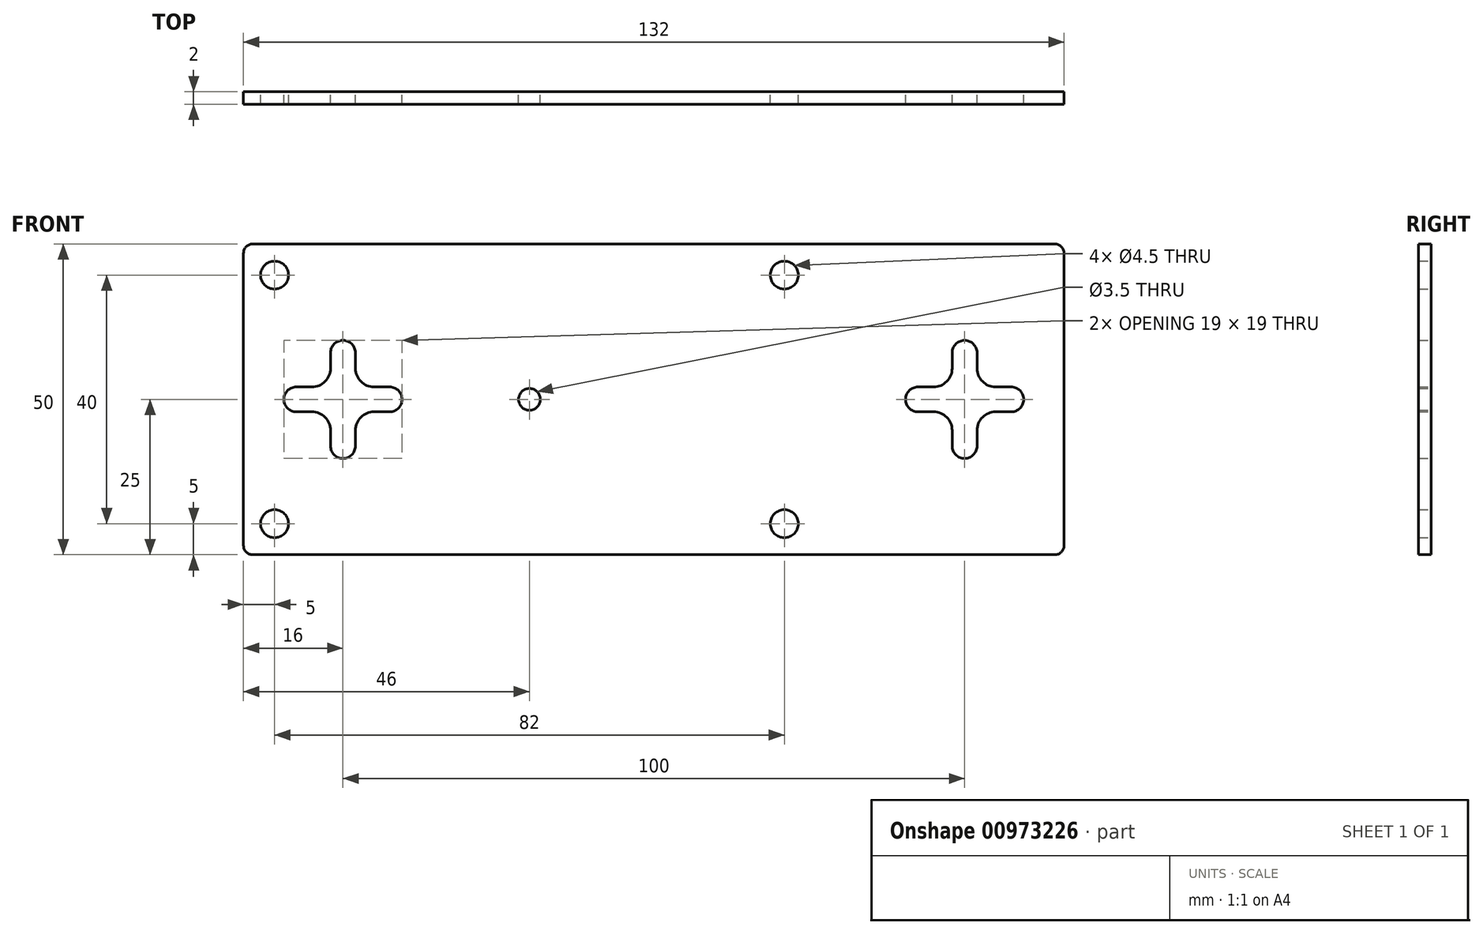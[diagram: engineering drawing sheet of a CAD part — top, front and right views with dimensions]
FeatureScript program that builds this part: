
annotation { "Feature Type Name" : "Feature", "Feature Type Description" : "" }
export const myFeature = defineFeature(function(context is Context, id is Id, definition is map)
    precondition{}
    {
        {
            var Q0;
            Q0=qCreatedBy(makeId("Front.planeOp"),FACE);
            var sketch = newSketch(context, id + "F0", { "sketchPlane" : qUnion([Q0])});
            skLineSegment(sketch, "E0.0", {"start": v(0, 0) * mm, "end": v(0, 50) * mm});
            skLineSegment(sketch, "E0.1", {"start": v(0, 0) * mm, "end": v(132, 0) * mm});
            skLineSegment(sketch, "E0.2", {"start": v(92, 0) * mm, "end": v(92, 50) * mm});
            skLineSegment(sketch, "E0.3", {"start": v(0, 50) * mm, "end": v(132, 50) * mm});
            skCircle(sketch, "E1", {"center": v(5, 45) * mm, "radius": 2.25 * mm});
            skCircle(sketch, "E2", {"center": v(87, 45) * mm, "radius": 2.25 * mm});
            skCircle(sketch, "E3", {"center": v(5, 5) * mm, "radius": 2.25 * mm});
            skCircle(sketch, "E4", {"center": v(87, 5) * mm, "radius": 2.25 * mm});
            skCircle(sketch, "E5", {"center": v(46, 25) * mm, "radius": 1.75 * mm});
            skLineSegment(sketch, "E6", {"start": v(132, 0) * mm, "end": v(132, 50) * mm});
            skLineSegment(sketch, "E7", {"start": v(16, 32.5) * mm, "end": v(16, 17.5) * mm});
            skLineSegment(sketch, "E8", {"start": v(8.5, 25) * mm, "end": v(23.5, 25) * mm});
            skArc(sketch, "E9.0.startCap", {"start": v(8.5, 23) * mm, "mid": v(6.5, 25) * mm, "end": v(8.5, 27) * mm});
            skArc(sketch, "E9.0.endCap", {"start": v(23.5, 27) * mm, "mid": v(25.5, 25) * mm, "end": v(23.5, 23) * mm});
            skLineSegment(sketch, "E9.0.left", {"start": v(8.5, 27) * mm, "end": v(23.5, 27) * mm});
            skLineSegment(sketch, "E9.0.right", {"start": v(8.5, 23) * mm, "end": v(23.5, 23) * mm});
            skArc(sketch, "E9.1.startCap", {"start": v(14, 32.5) * mm, "mid": v(16, 34.5) * mm, "end": v(18, 32.5) * mm});
            skArc(sketch, "E9.1.endCap", {"start": v(18, 17.5) * mm, "mid": v(16, 15.5) * mm, "end": v(14, 17.5) * mm});
            skLineSegment(sketch, "E9.1.left", {"start": v(18, 32.5) * mm, "end": v(18, 17.5) * mm});
            skLineSegment(sketch, "E9.1.right", {"start": v(14, 32.5) * mm, "end": v(14, 17.5) * mm});
            skLineSegment(sketch, "E10.1.0.0", {"start": v(114, 32.5) * mm, "end": v(114, 17.5) * mm});
            skLineSegment(sketch, "E10.1.0.1", {"start": v(108.5, 27) * mm, "end": v(123.5, 27) * mm});
            skArc(sketch, "E10.1.0.2", {"start": v(123.5, 27) * mm, "mid": v(125.5, 25) * mm, "end": v(123.5, 23) * mm});
            skArc(sketch, "E10.1.0.3", {"start": v(118, 17.5) * mm, "mid": v(116, 15.5) * mm, "end": v(114, 17.5) * mm});
            skLineSegment(sketch, "E10.1.0.4", {"start": v(116, 32.5) * mm, "end": v(116, 17.5) * mm});
            skLineSegment(sketch, "E10.1.0.5", {"start": v(108.5, 25) * mm, "end": v(123.5, 25) * mm});
            skLineSegment(sketch, "E10.1.0.6", {"start": v(108.5, 23) * mm, "end": v(123.5, 23) * mm});
            skArc(sketch, "E10.1.0.7", {"start": v(114, 32.5) * mm, "mid": v(116, 34.5) * mm, "end": v(118, 32.5) * mm});
            skArc(sketch, "E10.1.0.8", {"start": v(108.5, 23) * mm, "mid": v(106.5, 25) * mm, "end": v(108.5, 27) * mm});
            skLineSegment(sketch, "E10.1.0.9", {"start": v(118, 32.5) * mm, "end": v(118, 17.5) * mm});
            skLineSegment(sketch, "E10.direction1", {"start": v(14, 17.5) * mm, "end": v(114, 17.5) * mm, "construction": true});
            skLineSegment(sketch, "E11.filletArc", {"start": v(132, 50) * mm, "end": v(132, 50) * mm});
            skLineSegment(sketch, "E12.filletArc", {"start": v(132, 0) * mm, "end": v(132, 0) * mm});
            skSolve(sketch);
        }
        {
            var Q0;
            Q0=makeQuery(id+"F0.imprint","IMPRINT",FACE,{"disambiguationData":[TD([[makeQuery(id+"F0.imprint","IMPRINT",EDGE,{"derivedFrom":sQuery(id+"F0.wireOp",EDGE,"E1")}),-1.0]])]});
            var Q1;
            Q1=makeQuery(id+"F0.imprint","IMPRINT",FACE,{"disambiguationData":[TD([[makeQuery(id+"F0.imprint","IMPRINT",EDGE,{"derivedFrom":sQuery(id+"F0.wireOp",EDGE,"E3")}),-1.0]])]});
            var Q2;
            Q2=makeQuery(id+"F0.imprint","IMPRINT",FACE,{"disambiguationData":[TD([[makeQuery(id+"F0.imprint","IMPRINT",EDGE,{"derivedFrom":sQuery(id+"F0.wireOp",EDGE,"E4")}),-1.0]])]});
            var Q3;
            Q3=makeQuery(id+"F0.imprint","IMPRINT",FACE,{"disambiguationData":[TD([[makeQuery(id+"F0.imprint","IMPRINT",EDGE,{"derivedFrom":sQuery(id+"F0.wireOp",EDGE,"E2")}),-1.0]])]});
            var Q4;
            {var subQ0=sQuery(id+"F0.wireOp",EDGE,"xmzwrryO-BlZN-0bC2-PON8-yqqjyzBsKTHA");var subQ1=sQuery(id+"F0.wireOp",EDGE,"6Q67PZT9-bBxg-zhkt-OXOf-C5b4L4PpcKHw");var subQ2=makeQuery(id+"F0.imprint","INTERSECT",VERTEX,{"disambiguationData":[OD(0.0)],"derivedFrom":[subQ1,subQ0]});Q4=makeQuery(id+"F0.imprint","IMPRINT",FACE,{"disambiguationData":[TD([[makeQuery(id+"F0.imprint","IMPRINT",EDGE,{"disambiguationData":[TD([[subQ2,-1.0]])],"derivedFrom":subQ1}),-1.0]])]});}
            var Q5;
            {var subQ0=sQuery(id+"F0.wireOp",EDGE,"xmzwrryO-BlZN-0bC2-PON8-yqqjyzBsKTHA");var subQ1=sQuery(id+"F0.wireOp",EDGE,"6Q67PZT9-bBxg-zhkt-OXOf-C5b4L4PpcKHw");var subQ2=makeQuery(id+"F0.imprint","INTERSECT",VERTEX,{"disambiguationData":[OD(0.0)],"derivedFrom":[subQ1,subQ0]});Q5=makeQuery(id+"F0.imprint","IMPRINT",FACE,{"disambiguationData":[TD([[makeQuery(id+"F0.imprint","IMPRINT",EDGE,{"disambiguationData":[TD([[subQ2,-1.0]])],"derivedFrom":subQ1}),1.0]])]});}
            var Q6;
            {var subQ0=sQuery(id+"F0.wireOp",EDGE,"ZZCkcGhh-moAk-lj8j-4bvt-TYEpWencMZMl");var subQ1=sQuery(id+"F0.wireOp",EDGE,"NE1wQv6m-4w3k-G8xB-BjyB-1MqrszNTXdfy");var subQ2=makeQuery(id+"F0.imprint","INTERSECT",VERTEX,{"disambiguationData":[OD(0.0)],"derivedFrom":[subQ1,subQ0]});Q6=makeQuery(id+"F0.imprint","IMPRINT",FACE,{"disambiguationData":[TD([[makeQuery(id+"F0.imprint","IMPRINT",EDGE,{"disambiguationData":[TD([[subQ2,-1.0]])],"derivedFrom":subQ1}),-1.0]])]});}
            var Q7;
            {var subQ0=sQuery(id+"F0.wireOp",EDGE,"ZZCkcGhh-moAk-lj8j-4bvt-TYEpWencMZMl");var subQ1=sQuery(id+"F0.wireOp",EDGE,"NE1wQv6m-4w3k-G8xB-BjyB-1MqrszNTXdfy");var subQ2=makeQuery(id+"F0.imprint","INTERSECT",VERTEX,{"disambiguationData":[OD(0.0)],"derivedFrom":[subQ1,subQ0]});Q7=makeQuery(id+"F0.imprint","IMPRINT",FACE,{"disambiguationData":[TD([[makeQuery(id+"F0.imprint","IMPRINT",EDGE,{"disambiguationData":[TD([[subQ2,-1.0]])],"derivedFrom":subQ1}),1.0]])]});}
            var Q8;
            {var subQ0=sQuery(id+"F0.wireOp",EDGE,"5zX6bmv4-brnL-wLrf-yGTW-631ojesh5KmC");var subQ1=sQuery(id+"F0.wireOp",EDGE,"6Q67PZT9-bBxg-zhkt-OXOf-C5b4L4PpcKHw");var subQ2=makeQuery(id+"F0.imprint","INTERSECT",VERTEX,{"disambiguationData":[OD(0.0)],"derivedFrom":[subQ1,subQ0]});Q8=makeQuery(id+"F0.imprint","IMPRINT",FACE,{"disambiguationData":[TD([[makeQuery(id+"F0.imprint","IMPRINT",EDGE,{"disambiguationData":[TD([[subQ2,1.0]])],"derivedFrom":subQ1}),1.0]])]});}
            var Q9;
            {var subQ0=sQuery(id+"F0.wireOp",EDGE,"5zX6bmv4-brnL-wLrf-yGTW-631ojesh5KmC");var subQ1=sQuery(id+"F0.wireOp",EDGE,"6Q67PZT9-bBxg-zhkt-OXOf-C5b4L4PpcKHw");var subQ2=makeQuery(id+"F0.imprint","INTERSECT",VERTEX,{"disambiguationData":[OD(0.0)],"derivedFrom":[subQ1,subQ0]});Q9=makeQuery(id+"F0.imprint","IMPRINT",FACE,{"disambiguationData":[TD([[makeQuery(id+"F0.imprint","IMPRINT",EDGE,{"disambiguationData":[TD([[subQ2,1.0]])],"derivedFrom":subQ1}),-1.0]])]});}
            var Q10;
            {var subQ3=sQuery(id+"F0.wireOp",EDGE,"5zX6bmv4-brnL-wLrf-yGTW-631ojesh5KmC");var subQ5=sQuery(id+"F0.wireOp",EDGE,"6Q67PZT9-bBxg-zhkt-OXOf-C5b4L4PpcKHw");var subQ6=makeQuery(id+"F0.imprint","INTERSECT",VERTEX,{"disambiguationData":[OD(0.0)],"derivedFrom":[subQ5,subQ3]});Q10=makeQuery(id+"F0.imprint","IMPRINT",FACE,{"disambiguationData":[TD([[makeQuery(id+"F0.imprint","IMPRINT",EDGE,{"disambiguationData":[TD([[subQ6,-1.0]])],"derivedFrom":subQ5}),-1.0]])]});}
            var Q11;
            {var subQ3=sQuery(id+"F0.wireOp",EDGE,"5zX6bmv4-brnL-wLrf-yGTW-631ojesh5KmC");var subQ5=sQuery(id+"F0.wireOp",EDGE,"6Q67PZT9-bBxg-zhkt-OXOf-C5b4L4PpcKHw");var subQ6=makeQuery(id+"F0.imprint","INTERSECT",VERTEX,{"disambiguationData":[OD(0.0)],"derivedFrom":[subQ5,subQ3]});Q11=makeQuery(id+"F0.imprint","IMPRINT",FACE,{"disambiguationData":[TD([[makeQuery(id+"F0.imprint","IMPRINT",EDGE,{"disambiguationData":[TD([[subQ6,-1.0]])],"derivedFrom":subQ5}),1.0]])]});}
            var Q12;
            {var subQ0=sQuery(id+"F0.wireOp",EDGE,"E5");var subQ5=sQuery(id+"F0.wireOp",EDGE,"6Q67PZT9-bBxg-zhkt-OXOf-C5b4L4PpcKHw");var subQ6=makeQuery(id+"F0.imprint","INTERSECT",VERTEX,{"disambiguationData":[OD(1.0)],"derivedFrom":[subQ5,subQ0]});Q12=makeQuery(id+"F0.imprint","IMPRINT",FACE,{"disambiguationData":[TD([[makeQuery(id+"F0.imprint","IMPRINT",EDGE,{"disambiguationData":[TD([[subQ6,-1.0]])],"derivedFrom":subQ5}),1.0]])]});}
            var Q13;
            {var subQ0=sQuery(id+"F0.wireOp",EDGE,"E5");var subQ5=sQuery(id+"F0.wireOp",EDGE,"6Q67PZT9-bBxg-zhkt-OXOf-C5b4L4PpcKHw");var subQ7=makeQuery(id+"F0.imprint","INTERSECT",VERTEX,{"disambiguationData":[OD(1.0)],"derivedFrom":[subQ5,subQ0]});Q13=makeQuery(id+"F0.imprint","IMPRINT",FACE,{"disambiguationData":[TD([[makeQuery(id+"F0.imprint","IMPRINT",EDGE,{"disambiguationData":[TD([[subQ7,-1.0]])],"derivedFrom":subQ5}),-1.0]])]});}
            var Q14;
            {var subQ0=sQuery(id+"F0.wireOp",EDGE,"5zX6bmv4-brnL-wLrf-yGTW-631ojesh5KmC");var subQ1=sQuery(id+"F0.wireOp",EDGE,"6Q67PZT9-bBxg-zhkt-OXOf-C5b4L4PpcKHw");var subQ2=makeQuery(id+"F0.imprint","INTERSECT",VERTEX,{"disambiguationData":[OD(1.0)],"derivedFrom":[subQ1,subQ0]});Q14=makeQuery(id+"F0.imprint","IMPRINT",FACE,{"disambiguationData":[TD([[makeQuery(id+"F0.imprint","IMPRINT",EDGE,{"disambiguationData":[TD([[subQ2,-1.0]])],"derivedFrom":subQ1}),-1.0]])]});}
            var Q15;
            {var subQ0=sQuery(id+"F0.wireOp",EDGE,"5zX6bmv4-brnL-wLrf-yGTW-631ojesh5KmC");var subQ1=sQuery(id+"F0.wireOp",EDGE,"6Q67PZT9-bBxg-zhkt-OXOf-C5b4L4PpcKHw");var subQ2=makeQuery(id+"F0.imprint","INTERSECT",VERTEX,{"disambiguationData":[OD(1.0)],"derivedFrom":[subQ1,subQ0]});Q15=makeQuery(id+"F0.imprint","IMPRINT",FACE,{"disambiguationData":[TD([[makeQuery(id+"F0.imprint","IMPRINT",EDGE,{"disambiguationData":[TD([[subQ2,-1.0]])],"derivedFrom":subQ1}),1.0]])]});}
            var Q16;
            {var subQ0=sQuery(id+"F0.wireOp",EDGE,"qFN6vZkK-eyPu-iBXI-5w6p-NcDML7FWDEbE");var subQ1=sQuery(id+"F0.wireOp",EDGE,"NE1wQv6m-4w3k-G8xB-BjyB-1MqrszNTXdfy");var subQ2=makeQuery(id+"F0.imprint","INTERSECT",VERTEX,{"disambiguationData":[OD(1.0)],"derivedFrom":[subQ1,subQ0]});Q16=makeQuery(id+"F0.imprint","IMPRINT",FACE,{"disambiguationData":[TD([[makeQuery(id+"F0.imprint","IMPRINT",EDGE,{"disambiguationData":[TD([[subQ2,-1.0]])],"derivedFrom":subQ1}),1.0]])]});}
            var Q17;
            {var subQ0=sQuery(id+"F0.wireOp",EDGE,"qFN6vZkK-eyPu-iBXI-5w6p-NcDML7FWDEbE");var subQ1=sQuery(id+"F0.wireOp",EDGE,"NE1wQv6m-4w3k-G8xB-BjyB-1MqrszNTXdfy");var subQ2=makeQuery(id+"F0.imprint","INTERSECT",VERTEX,{"disambiguationData":[OD(1.0)],"derivedFrom":[subQ1,subQ0]});Q17=makeQuery(id+"F0.imprint","IMPRINT",FACE,{"disambiguationData":[TD([[makeQuery(id+"F0.imprint","IMPRINT",EDGE,{"disambiguationData":[TD([[subQ2,-1.0]])],"derivedFrom":subQ1}),-1.0]])]});}
            var Q18;
            {var subQ0=sQuery(id+"F0.wireOp",EDGE,"xmzwrryO-BlZN-0bC2-PON8-yqqjyzBsKTHA");var subQ1=sQuery(id+"F0.wireOp",EDGE,"6Q67PZT9-bBxg-zhkt-OXOf-C5b4L4PpcKHw");var subQ2=makeQuery(id+"F0.imprint","INTERSECT",VERTEX,{"disambiguationData":[OD(1.0)],"derivedFrom":[subQ1,subQ0]});Q18=makeQuery(id+"F0.imprint","IMPRINT",FACE,{"disambiguationData":[TD([[makeQuery(id+"F0.imprint","IMPRINT",EDGE,{"disambiguationData":[TD([[subQ2,1.0]])],"derivedFrom":subQ1}),-1.0]])]});}
            var Q19;
            {var subQ0=sQuery(id+"F0.wireOp",EDGE,"xmzwrryO-BlZN-0bC2-PON8-yqqjyzBsKTHA");var subQ1=sQuery(id+"F0.wireOp",EDGE,"6Q67PZT9-bBxg-zhkt-OXOf-C5b4L4PpcKHw");var subQ2=makeQuery(id+"F0.imprint","INTERSECT",VERTEX,{"disambiguationData":[OD(1.0)],"derivedFrom":[subQ1,subQ0]});Q19=makeQuery(id+"F0.imprint","IMPRINT",FACE,{"disambiguationData":[TD([[makeQuery(id+"F0.imprint","IMPRINT",EDGE,{"disambiguationData":[TD([[subQ2,1.0]])],"derivedFrom":subQ1}),1.0]])]});}
            var Q20;
            {var subQ12=sQuery(id+"F0.wireOp",EDGE,"E0.2");Q20=makeQuery(id+"F0.imprint","IMPRINT",FACE,{"disambiguationData":[TD([[makeQuery(id+"F0.imprint","IMPRINT",EDGE,{"derivedFrom":subQ12}),-1.0]])]});}
            extrude(context, id + "F1", {"entities" : qUnion([Q0, Q1, Q2, Q3, Q4, Q5, Q6, Q7, Q8, Q9, Q10, Q11, Q12, Q13, Q14, Q15, Q16, Q17, Q18, Q19, Q20]), "depth" : 2 * mm, "offsetDistance" : 25 * mm});
        }
        {
            var Q0;
            Q0=makeQuery(id+"F1.opExtrude","SWEPT_EDGE",EDGE,{"disambiguationData":[OSD([sQuery(id+"F0.wireOp",EDGE,"E9.0.left"),sQuery(id+"F0.wireOp",EDGE,"E9.1.right")])]});
            var Q1;
            Q1=makeQuery(id+"F1.opExtrude","SWEPT_EDGE",EDGE,{"disambiguationData":[OSD([sQuery(id+"F0.wireOp",EDGE,"E9.0.right"),sQuery(id+"F0.wireOp",EDGE,"E9.1.right")])]});
            var Q2;
            Q2=makeQuery(id+"F1.opExtrude","SWEPT_EDGE",EDGE,{"disambiguationData":[OSD([sQuery(id+"F0.wireOp",EDGE,"E9.0.left"),sQuery(id+"F0.wireOp",EDGE,"E9.1.left")])]});
            var Q3;
            Q3=makeQuery(id+"F1.opExtrude","SWEPT_EDGE",EDGE,{"disambiguationData":[OSD([sQuery(id+"F0.wireOp",EDGE,"E9.0.right"),sQuery(id+"F0.wireOp",EDGE,"E9.1.left")])]});
            var Q4;
            Q4=makeQuery(id+"F1.opExtrude","SWEPT_EDGE",EDGE,{"disambiguationData":[OSD([sQuery(id+"F0.wireOp",EDGE,"E10.1.0.0"),sQuery(id+"F0.wireOp",EDGE,"E10.1.0.1")])]});
            var Q5;
            Q5=makeQuery(id+"F1.opExtrude","SWEPT_EDGE",EDGE,{"disambiguationData":[OSD([sQuery(id+"F0.wireOp",EDGE,"E10.1.0.1"),sQuery(id+"F0.wireOp",EDGE,"E10.1.0.9")])]});
            var Q6;
            Q6=makeQuery(id+"F1.opExtrude","SWEPT_EDGE",EDGE,{"disambiguationData":[OSD([sQuery(id+"F0.wireOp",EDGE,"E10.1.0.0"),sQuery(id+"F0.wireOp",EDGE,"E10.1.0.6")])]});
            var Q7;
            Q7=makeQuery(id+"F1.opExtrude","SWEPT_EDGE",EDGE,{"disambiguationData":[OSD([sQuery(id+"F0.wireOp",EDGE,"E10.1.0.6"),sQuery(id+"F0.wireOp",EDGE,"E10.1.0.9")])]});
            fillet(context, id + "F2", {"entities" : qUnion([Q0, Q1, Q2, Q3, Q4, Q5, Q6, Q7]), "radius" : 3 * mm, "tangentPropagation" : true, "allowEdgeOverflow" : false});
        }
        {
            var Q0;
            Q0=makeQuery(id+"F1.opExtrude","SWEPT_EDGE",EDGE,{"disambiguationData":[OSD([sQuery(id+"F0.wireOp",EDGE,"E0.0"),sQuery(id+"F0.wireOp",EDGE,"E0.3")])]});
            var Q1;
            Q1=makeQuery(id+"F1.opExtrude","SWEPT_EDGE",EDGE,{"disambiguationData":[OSD([sQuery(id+"F0.wireOp",EDGE,"E0.0"),sQuery(id+"F0.wireOp",EDGE,"E0.1")])]});
            var Q2;
            Q2=makeQuery(id+"F1.opExtrude","SWEPT_EDGE",EDGE,{"disambiguationData":[OSD([sQuery(id+"F0.wireOp",EDGE,"E0.1"),sQuery(id+"F0.wireOp",EDGE,"E6")])]});
            var Q3;
            Q3=makeQuery(id+"F1.opExtrude","SWEPT_EDGE",EDGE,{"disambiguationData":[OSD([sQuery(id+"F0.wireOp",EDGE,"E0.3"),sQuery(id+"F0.wireOp",EDGE,"E6")])]});
            fillet(context, id + "F3", {"entities" : qUnion([Q0, Q1, Q2, Q3]), "radius" : 1.5 * mm, "tangentPropagation" : true, "allowEdgeOverflow" : false});
        }
    });
